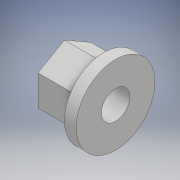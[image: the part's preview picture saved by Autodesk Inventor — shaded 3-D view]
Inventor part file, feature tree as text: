
AUTODESK INVENTOR PART (.ipt)
format: ipt  version: 2018 (Build 220112000, 112)  size: 113,664 bytes
history: native  units: mm
features: extrude x3, sketch x3
ambient origin geometry x8: Origin, YZ Plane, XZ Plane, XY Plane, X Axis, Y Axis, Z Axis, Center Point
bodies: Solid1 (feature_tree)
feature tree (6):
  extrude  "Extrusion1"  Depth=10.0mm TaperAngle=0.0deg
  extrude  "Extrusion2"  Depth=3.0mm TaperAngle=0.0deg
  extrude  "Extrusion3"  Depth=15.0mm TaperAngle=0.0deg
  sketch  "Sketch1"  dims[d0=7.75mm d1=10.0mm d2=0.0mm]
  sketch  "Sketch2"  dims[d3=20.0mm d4=3.0mm d5=0.0mm]
  sketch  "Sketch3"  dims[d6=7.25mm d7=15.0mm d8=0.0mm]
